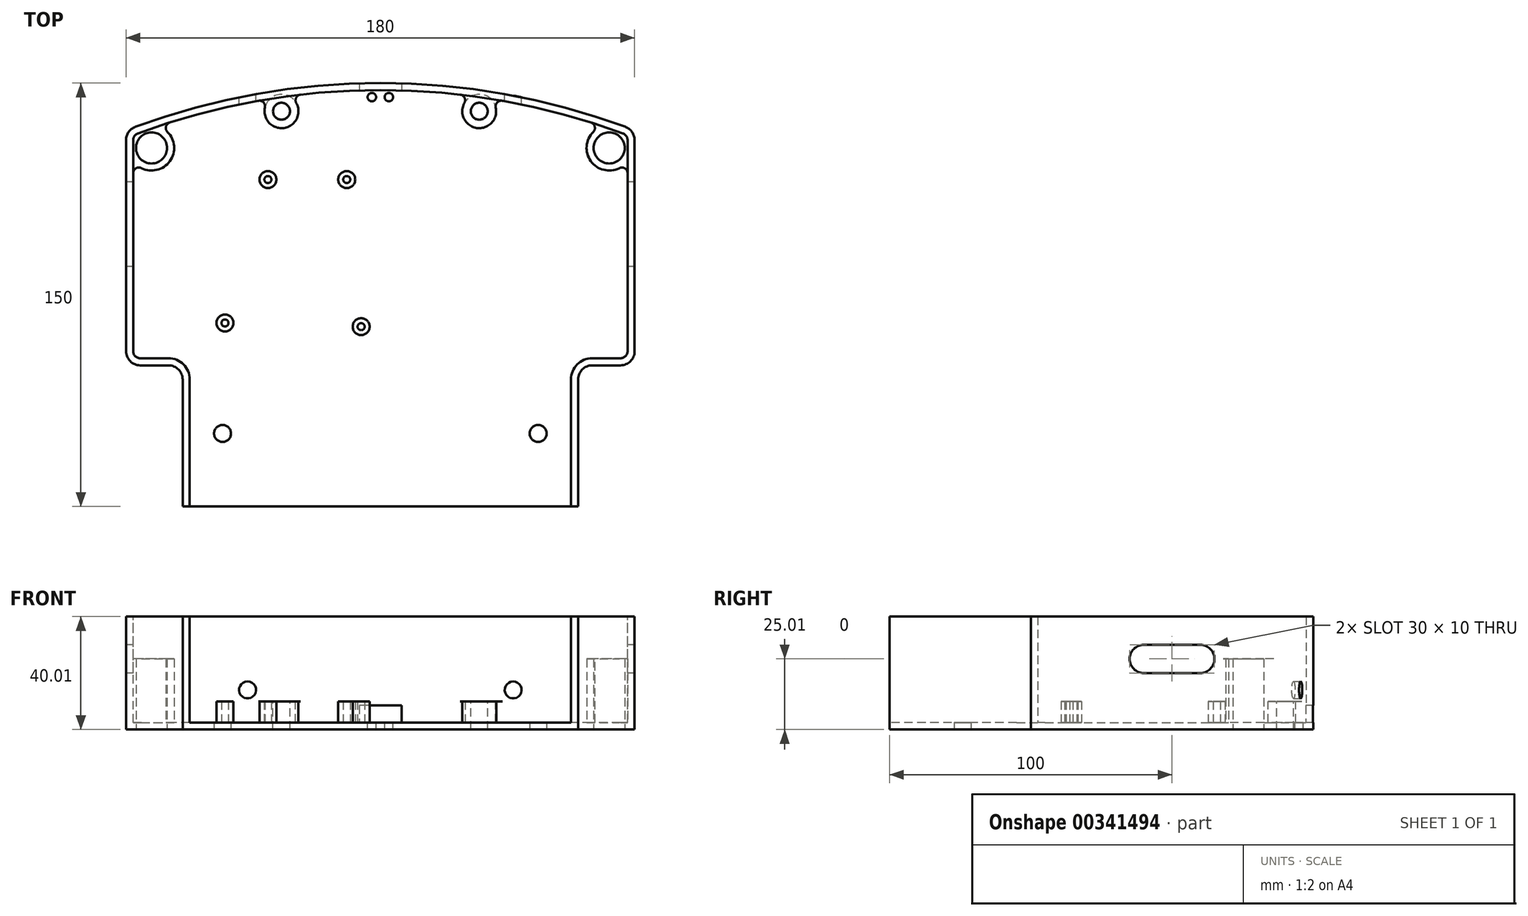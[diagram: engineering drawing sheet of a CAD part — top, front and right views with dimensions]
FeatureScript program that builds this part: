
annotation { "Feature Type Name" : "Feature", "Feature Type Description" : "" }
export const myFeature = defineFeature(function(context is Context, id is Id, definition is map)
    precondition{}
    {
        {
            var Q0;
            Q0=qCreatedBy(makeId("Top.planeOp"),FACE);
            var sketch = newSketch(context, id + "F0", { "sketchPlane" : qUnion([Q0])});
            skLineSegment(sketch, "E0.bottom", {"start": v(-90, -50) * mm, "end": v(90, -50) * mm});
            skLineSegment(sketch, "E0.top", {"start": v(-90, 100) * mm, "end": v(90, 100) * mm});
            skLineSegment(sketch, "E0.left", {"start": v(-90, -50) * mm, "end": v(-90, 100) * mm});
            skLineSegment(sketch, "E0.right", {"start": v(90, -50) * mm, "end": v(90, 100) * mm});
            skCircle(sketch, "E1", {"center": v(0, -150) * mm, "radius": 250 * mm});
            skSolve(sketch);
        }
        {
            var Q0;
            {var subQ4=sQuery(id+"F0.wireOp",EDGE,"E0.bottom");Q0=makeQuery(id+"F0.imprint","IMPRINT",FACE,{"disambiguationData":[TD([[makeQuery(id+"F0.imprint","IMPRINT",EDGE,{"derivedFrom":subQ4}),1.0]])]});}
            extrude(context, id + "F1", {"entities" : qUnion([Q0]), "depth" : 40 * mm});
        }
        {
            var Q0;
            Q0=qCreatedBy(makeId("Top.planeOp"),FACE);
            var sketch = newSketch(context, id + "F2", { "sketchPlane" : qUnion([Q0])});
            skLineSegment(sketch, "E2.bottom", {"start": v(-170, 0) * mm, "end": v(-70, 0) * mm});
            skLineSegment(sketch, "E2.top", {"start": v(-170, -200) * mm, "end": v(-70, -200) * mm});
            skLineSegment(sketch, "E2.left", {"start": v(-170, 0) * mm, "end": v(-170, -200) * mm});
            skLineSegment(sketch, "E2.right", {"start": v(-70, 0) * mm, "end": v(-70, -200) * mm});
            skLineSegment(sketch, "E3.bottom", {"start": v(170, 0) * mm, "end": v(70, 0) * mm});
            skLineSegment(sketch, "E3.top", {"start": v(170, -200) * mm, "end": v(70, -200) * mm});
            skLineSegment(sketch, "E3.left", {"start": v(170, 0) * mm, "end": v(170, -200) * mm});
            skLineSegment(sketch, "E3.right", {"start": v(70, 0) * mm, "end": v(70, -200) * mm});
            skSolve(sketch);
        }
        {
            var Q0;
            Q0=makeQuery(id+"F2.imprint","IMPRINT",FACE,{"disambiguationData":[TD([[makeQuery(id+"F2.imprint","IMPRINT",EDGE,{"derivedFrom":sQuery(id+"F2.wireOp",EDGE,"E2.bottom")}),-1.0]])]});
            var Q1;
            Q1=makeQuery(id+"F2.imprint","IMPRINT",FACE,{"disambiguationData":[TD([[makeQuery(id+"F2.imprint","IMPRINT",EDGE,{"derivedFrom":sQuery(id+"F2.wireOp",EDGE,"E3.bottom")}),1.0]])]});
            extrude(context, id + "F3", {"entities" : qUnion([Q0, Q1]), "operationType" : NewBodyOperationType.REMOVE, "depth" : 100 * mm});
        }
        {
            var Q0;
            Q0=makeQuery(id+"F1.opExtrude","SWEPT_EDGE",EDGE,{"disambiguationData":[OSD([sQuery(id+"F0.wireOp",EDGE,"E0.left"),sQuery(id+"F0.wireOp",EDGE,"E1")])]});
            var Q1;
            Q1=makeQuery(id+"F1.opExtrude","SWEPT_EDGE",EDGE,{"disambiguationData":[OSD([sQuery(id+"F0.wireOp",EDGE,"E0.right"),sQuery(id+"F0.wireOp",EDGE,"E1")])]});
            var Q2;
            Q2=makeQuery(id+"F3.boolean.opBoolean","INTERSECT",EDGE,{"derivedFrom":[makeQuery(id+"F1.opExtrude","SWEPT_FACE",FACE,{"disambiguationData":[OSD([sQuery(id+"F0.wireOp",EDGE,"E0.right")])]}),makeQuery(id+"F3.opExtrude","SWEPT_FACE",FACE,{"disambiguationData":[OSD([sQuery(id+"F2.wireOp",EDGE,"E3.bottom")])]})]});
            var Q3;
            Q3=makeQuery(id+"F3.boolean.opBoolean","COPY",EDGE,{"derivedFrom":makeQuery(id+"F3.opExtrude","SWEPT_EDGE",EDGE,{"disambiguationData":[OSD([sQuery(id+"F2.wireOp",EDGE,"E3.bottom"),sQuery(id+"F2.wireOp",EDGE,"E3.right")])]})});
            var Q4;
            Q4=makeQuery(id+"F3.boolean.opBoolean","INTERSECT",EDGE,{"derivedFrom":[makeQuery(id+"F1.opExtrude","SWEPT_FACE",FACE,{"disambiguationData":[OSD([sQuery(id+"F0.wireOp",EDGE,"E0.left")])]}),makeQuery(id+"F3.opExtrude","SWEPT_FACE",FACE,{"disambiguationData":[OSD([sQuery(id+"F2.wireOp",EDGE,"E2.bottom")])]})]});
            var Q5;
            Q5=makeQuery(id+"F3.boolean.opBoolean","COPY",EDGE,{"derivedFrom":makeQuery(id+"F3.opExtrude","SWEPT_EDGE",EDGE,{"disambiguationData":[OSD([sQuery(id+"F2.wireOp",EDGE,"E2.bottom"),sQuery(id+"F2.wireOp",EDGE,"E2.right")])]})});
            fillet(context, id + "F4", {"entities" : qUnion([Q0, Q1, Q2, Q3, Q4, Q5]), "radius" : 5 * mm, "tangentPropagation" : true, "allowEdgeOverflow" : false});
        }
        {
            var Q0;
            Q0=makeQuery(id+"F1.opExtrude","CAP_FACE",FACE,{"disambiguationData":[OSD([sQuery(id+"F0.wireOp",EDGE,"E0.bottom"),sQuery(id+"F0.wireOp",EDGE,"E0.left"),sQuery(id+"F0.wireOp",EDGE,"E0.right"),sQuery(id+"F0.wireOp",EDGE,"E1")])],"isStart":false});
            var Q1;
            Q1=makeQuery(id+"F1.opExtrude","SWEPT_FACE",FACE,{"disambiguationData":[OSD([sQuery(id+"F0.wireOp",EDGE,"E0.bottom")])]});
            shell(context, id + "F5", {"entities" : qUnion([Q0, Q1]), "thickness" : 2.5 * mm});
        }
        {
            var Q0;
            Q0=qCreatedBy(makeId("Top.planeOp"),FACE);
            var sketch = newSketch(context, id + "F6", { "sketchPlane" : qUnion([Q0])});
            skCircle(sketch, "E4", {"center": v(-55.86, -24.14) * mm, "radius": 3 * mm});
            skCircle(sketch, "E5", {"center": v(55.86, -24.14) * mm, "radius": 3 * mm});
            skLineSegment(sketch, "E6", {"start": v(0, -80) * mm, "end": v(-55.86, -24.14) * mm, "construction": true});
            skLineSegment(sketch, "E7", {"start": v(0, -80) * mm, "end": v(55.86, -24.14) * mm, "construction": true});
            skSolve(sketch);
        }
        {
            var Q0;
            Q0=qSketchRegion(id+"F6",true);
            extrude(context, id + "F7", {"entities" : qUnion([Q0]), "operationType" : NewBodyOperationType.REMOVE, "depth" : 25 * mm});
        }
        {
            var Q0;
            Q0=qCreatedBy(makeId("Top.planeOp"),FACE);
            var sketch = newSketch(context, id + "F8", { "sketchPlane" : qUnion([Q0])});
            skCircle(sketch, "E8", {"center": v(-81, 77) * mm, "radius": 8 * mm});
            skCircle(sketch, "E9", {"center": v(81, 77) * mm, "radius": 8 * mm});
            skSolve(sketch);
        }
        {
            var Q0;
            Q0=qSketchRegion(id+"F8",true);
            extrude(context, id + "F9", {"entities" : qUnion([Q0]), "operationType" : NewBodyOperationType.ADD, "depth" : 25 * mm});
        }
        {
            var Q0;
            Q0=qCreatedBy(makeId("Top.planeOp"),FACE);
            var sketch = newSketch(context, id + "F10", { "sketchPlane" : qUnion([Q0])});
            skCircle(sketch, "E10", {"center": v(-81, 77) * mm, "radius": 5.5 * mm});
            skCircle(sketch, "E11", {"center": v(81, 77) * mm, "radius": 5.5 * mm});
            skSolve(sketch);
        }
        {
            var Q0;
            Q0=qSketchRegion(id+"F10",true);
            extrude(context, id + "F11", {"entities" : qUnion([Q0]), "operationType" : NewBodyOperationType.REMOVE, "depth" : 25 * mm});
        }
        {
            var Q0;
            Q0=qCreatedBy(makeId("Top.planeOp"),FACE);
            var sketch = newSketch(context, id + "F12", { "sketchPlane" : qUnion([Q0])});
            skCircle(sketch, "E12", {"center": v(-55, 15) * mm, "radius": 3 * mm});
            skCircle(sketch, "E13", {"center": v(-55, 15) * mm, "radius": 1.25 * mm});
            skCircle(sketch, "E14", {"center": v(-39.8, 65.8) * mm, "radius": 1.25 * mm});
            skCircle(sketch, "E15", {"center": v(-39.8, 65.8) * mm, "radius": 3 * mm});
            skCircle(sketch, "E16", {"center": v(-11.9, 65.8) * mm, "radius": 1.25 * mm});
            skCircle(sketch, "E17", {"center": v(-11.9, 65.8) * mm, "radius": 3 * mm});
            skCircle(sketch, "E18", {"center": v(-6.8, 13.7) * mm, "radius": 1.25 * mm});
            skCircle(sketch, "E19", {"center": v(-6.8, 13.7) * mm, "radius": 3 * mm});
            skSolve(sketch);
        }
        {
            var Q0;
            Q0=qSketchRegion(id+"F12",true);
            extrude(context, id + "F13", {"entities" : qUnion([Q0]), "operationType" : NewBodyOperationType.ADD, "depth" : 10 * mm});
        }
        {
            var Q0;
            Q0=qCreatedBy(makeId("Front.planeOp"),FACE);
            var sketch = newSketch(context, id + "F14", { "sketchPlane" : qUnion([Q0])});
            skCircle(sketch, "E20", {"center": v(47, 14) * mm, "radius": 3 * mm});
            skCircle(sketch, "E21", {"center": v(-47, 14) * mm, "radius": 3 * mm});
            skSolve(sketch);
        }
        {
            var Q0;
            Q0=qSketchRegion(id+"F14",true);
            extrude(context, id + "F15", {"entities" : qUnion([Q0]), "operationType" : NewBodyOperationType.REMOVE, "endBound" : BoundingType.SYMMETRIC, "depth" : 300 * mm});
        }
        {
            var Q0;
            Q0=qCreatedBy(makeId("Front.planeOp"),FACE);
            var sketch = newSketch(context, id + "F16", { "sketchPlane" : qUnion([Q0])});
            skLineSegment(sketch, "E22.bottom", {"start": v(7.5, 8.5) * mm, "end": v(-7.5, 8.5) * mm});
            skLineSegment(sketch, "E22.top", {"start": v(7.5, 2.5) * mm, "end": v(-7.5, 2.5) * mm});
            skLineSegment(sketch, "E22.left", {"start": v(7.5, 8.5) * mm, "end": v(7.5, 2.5) * mm});
            skLineSegment(sketch, "E22.right", {"start": v(-7.5, 8.5) * mm, "end": v(-7.5, 2.5) * mm});
            skSolve(sketch);
        }
        {
            var Q0;
            Q0=makeQuery(id+"F16.imprint","IMPRINT",FACE,{"disambiguationData":[TD([[makeQuery(id+"F16.imprint","IMPRINT",EDGE,{"derivedFrom":sQuery(id+"F16.wireOp",EDGE,"E22.bottom")}),1.0]])]});
            extrude(context, id + "F17", {"entities" : qUnion([Q0]), "operationType" : NewBodyOperationType.REMOVE, "oppositeDirection" : true, "depth" : 250 * mm, "hasSecondDirection" : true, "secondDirectionOppositeDirection" : true, "secondDirectionDepth" : 41.95 * mm});
        }
        {
            var Q0;
            Q0=qCreatedBy(makeId("Top.planeOp"),FACE);
            var sketch = newSketch(context, id + "F18", { "sketchPlane" : qUnion([Q0])});
            skCircle(sketch, "E23", {"center": v(3, 95) * mm, "radius": 1.5 * mm});
            skCircle(sketch, "E24", {"center": v(-3, 95) * mm, "radius": 1.5 * mm});
            skSolve(sketch);
        }
        {
            var Q0;
            Q0=makeQuery(id+"F18.imprint","IMPRINT",FACE,{"disambiguationData":[TD([[makeQuery(id+"F18.imprint","IMPRINT",EDGE,{"derivedFrom":sQuery(id+"F18.wireOp",EDGE,"E24")}),1.0]])]});
            var Q1;
            Q1=makeQuery(id+"F18.imprint","IMPRINT",FACE,{"disambiguationData":[TD([[makeQuery(id+"F18.imprint","IMPRINT",EDGE,{"derivedFrom":sQuery(id+"F18.wireOp",EDGE,"E23")}),1.0]])]});
            extrude(context, id + "F19", {"entities" : qUnion([Q0, Q1]), "operationType" : NewBodyOperationType.REMOVE, "endBound" : BoundingType.SYMMETRIC, "oppositeDirection" : true, "depth" : 25 * mm});
        }
        {
            var Q0;
            Q0=qCreatedBy(makeId("Top.planeOp"),FACE);
            var sketch = newSketch(context, id + "F20", { "sketchPlane" : qUnion([Q0])});
            skCircle(sketch, "E25", {"center": v(-35, 90) * mm, "radius": 6 * mm});
            skCircle(sketch, "E26", {"center": v(35, 90) * mm, "radius": 6 * mm});
            skSolve(sketch);
        }
        {
            var Q0;
            Q0=qSketchRegion(id+"F20",true);
            extrude(context, id + "F21", {"entities" : qUnion([Q0]), "operationType" : NewBodyOperationType.ADD, "oppositeDirection" : true, "depth" : 0.01 * mm, "hasSecondDirection" : true, "secondDirectionOppositeDirection" : false, "secondDirectionDepth" : 10 * mm});
        }
        {
            var Q0;
            Q0=makeQuery(id+"F1.opExtrude","CAP_FACE",FACE,{"disambiguationData":[OSD([sQuery(id+"F0.wireOp",EDGE,"E0.bottom"),sQuery(id+"F0.wireOp",EDGE,"E0.left"),sQuery(id+"F0.wireOp",EDGE,"E0.right"),sQuery(id+"F0.wireOp",EDGE,"E1")])],"isStart":true});
            var sketch = newSketch(context, id + "F22", { "sketchPlane" : qUnion([Q0])});
            skCircle(sketch, "E27", {"center": v(-35, -90) * mm, "radius": 3 * mm});
            skCircle(sketch, "E28", {"center": v(35, -90) * mm, "radius": 3 * mm});
            skSolve(sketch);
        }
        {
            var Q0;
            Q0=qSketchRegion(id+"F22",true);
            extrude(context, id + "F23", {"entities" : qUnion([Q0]), "operationType" : NewBodyOperationType.REMOVE, "endBound" : BoundingType.SYMMETRIC, "depth" : 25 * mm});
        }
        {
            var Q0;
            Q0=makeQuery(id+"F9.boolean.opBoolean","INTERSECT",EDGE,{"derivedFrom":[makeQuery(id+"F5.opShell","OFFSET_FACE",FACE,{"disambiguationData":[OSD([sQuery(id+"F0.wireOp",EDGE,"E0.left")])]}),makeQuery(id+"F9.opExtrude","SWEPT_FACE",FACE,{"disambiguationData":[OSD([sQuery(id+"F8.wireOp",EDGE,"E8")])]})]});
            var Q1;
            Q1=makeQuery(id+"F9.boolean.opBoolean","INTERSECT",EDGE,{"derivedFrom":[makeQuery(id+"F5.opShell","OFFSET_FACE",FACE,{"disambiguationData":[OSD([sQuery(id+"F0.wireOp",EDGE,"E1")])]}),makeQuery(id+"F9.opExtrude","SWEPT_FACE",FACE,{"disambiguationData":[OSD([sQuery(id+"F8.wireOp",EDGE,"E8")])]})]});
            var Q2;
            Q2=makeQuery(id+"F21.boolean.opBoolean","INTERSECT",EDGE,{"disambiguationData":[OD(0.0)],"derivedFrom":[makeQuery(id+"F5.opShell","OFFSET_FACE",FACE,{"disambiguationData":[OSD([sQuery(id+"F0.wireOp",EDGE,"E1")])]}),makeQuery(id+"F21.opExtrude","SWEPT_FACE",FACE,{"disambiguationData":[OSD([sQuery(id+"F20.wireOp",EDGE,"E25")])]})]});
            var Q3;
            Q3=makeQuery(id+"F21.boolean.opBoolean","INTERSECT",EDGE,{"disambiguationData":[OD(1.0)],"derivedFrom":[makeQuery(id+"F5.opShell","OFFSET_FACE",FACE,{"disambiguationData":[OSD([sQuery(id+"F0.wireOp",EDGE,"E1")])]}),makeQuery(id+"F21.opExtrude","SWEPT_FACE",FACE,{"disambiguationData":[OSD([sQuery(id+"F20.wireOp",EDGE,"E25")])]})]});
            var Q4;
            Q4=makeQuery(id+"F21.boolean.opBoolean","INTERSECT",EDGE,{"disambiguationData":[OD(1.0)],"derivedFrom":[makeQuery(id+"F5.opShell","OFFSET_FACE",FACE,{"disambiguationData":[OSD([sQuery(id+"F0.wireOp",EDGE,"E1")])]}),makeQuery(id+"F21.opExtrude","SWEPT_FACE",FACE,{"disambiguationData":[OSD([sQuery(id+"F20.wireOp",EDGE,"E26")])]})]});
            var Q5;
            Q5=makeQuery(id+"F21.boolean.opBoolean","INTERSECT",EDGE,{"disambiguationData":[OD(0.0)],"derivedFrom":[makeQuery(id+"F5.opShell","OFFSET_FACE",FACE,{"disambiguationData":[OSD([sQuery(id+"F0.wireOp",EDGE,"E1")])]}),makeQuery(id+"F21.opExtrude","SWEPT_FACE",FACE,{"disambiguationData":[OSD([sQuery(id+"F20.wireOp",EDGE,"E26")])]})]});
            var Q6;
            Q6=makeQuery(id+"F9.boolean.opBoolean","INTERSECT",EDGE,{"derivedFrom":[makeQuery(id+"F5.opShell","OFFSET_FACE",FACE,{"disambiguationData":[OSD([sQuery(id+"F0.wireOp",EDGE,"E1")])]}),makeQuery(id+"F9.opExtrude","SWEPT_FACE",FACE,{"disambiguationData":[OSD([sQuery(id+"F8.wireOp",EDGE,"E9")])]})]});
            var Q7;
            Q7=makeQuery(id+"F9.boolean.opBoolean","INTERSECT",EDGE,{"derivedFrom":[makeQuery(id+"F5.opShell","OFFSET_FACE",FACE,{"disambiguationData":[OSD([sQuery(id+"F0.wireOp",EDGE,"E0.right")])]}),makeQuery(id+"F9.opExtrude","SWEPT_FACE",FACE,{"disambiguationData":[OSD([sQuery(id+"F8.wireOp",EDGE,"E9")])]})]});
            fillet(context, id + "F24", {"entities" : qUnion([Q0, Q1, Q2, Q3, Q4, Q5, Q6, Q7]), "radius" : 2 * mm, "tangentPropagation" : true, "allowEdgeOverflow" : false});
        }
        {
            var Q0;
            Q0=qCreatedBy(makeId("Right.planeOp"),FACE);
            var sketch = newSketch(context, id + "F25", { "sketchPlane" : qUnion([Q0])});
            skLineSegment(sketch, "E29.bottom", {"start": v(40, 30) * mm, "end": v(60, 30) * mm});
            skLineSegment(sketch, "E29.top", {"start": v(40, 20) * mm, "end": v(60, 20) * mm});
            skLineSegment(sketch, "E29.left", {"start": v(40, 30) * mm, "end": v(40, 20) * mm});
            skLineSegment(sketch, "E29.right", {"start": v(60, 30) * mm, "end": v(60, 20) * mm});
            skCircle(sketch, "E30", {"center": v(40, 25) * mm, "radius": 5 * mm});
            skCircle(sketch, "E31", {"center": v(60, 25) * mm, "radius": 5 * mm});
            skSolve(sketch);
        }
        {
            var Q0;
            {var subQ0=sQuery(id+"F25.wireOp",EDGE,"E29.left");Q0=makeQuery(id+"F25.imprint","IMPRINT",FACE,{"disambiguationData":[TD([[makeQuery(id+"F25.imprint","IMPRINT",EDGE,{"derivedFrom":subQ0}),-1.0]])]});}
            var Q1;
            {var subQ0=sQuery(id+"F25.wireOp",EDGE,"E29.right");Q1=makeQuery(id+"F25.imprint","IMPRINT",FACE,{"disambiguationData":[TD([[makeQuery(id+"F25.imprint","IMPRINT",EDGE,{"derivedFrom":subQ0}),1.0]])]});}
            var Q2;
            {var subQ0=sQuery(id+"F25.wireOp",EDGE,"E29.bottom");Q2=makeQuery(id+"F25.imprint","IMPRINT",FACE,{"disambiguationData":[TD([[makeQuery(id+"F25.imprint","IMPRINT",EDGE,{"derivedFrom":subQ0}),-1.0]])]});}
            var Q3;
            {var subQ0=sQuery(id+"F25.wireOp",EDGE,"E29.left");Q3=makeQuery(id+"F25.imprint","IMPRINT",FACE,{"disambiguationData":[TD([[makeQuery(id+"F25.imprint","IMPRINT",EDGE,{"derivedFrom":subQ0}),1.0]])]});}
            var Q4;
            {var subQ0=sQuery(id+"F25.wireOp",EDGE,"E29.right");Q4=makeQuery(id+"F25.imprint","IMPRINT",FACE,{"disambiguationData":[TD([[makeQuery(id+"F25.imprint","IMPRINT",EDGE,{"derivedFrom":subQ0}),-1.0]])]});}
            extrude(context, id + "F26", {"entities" : qUnion([Q0, Q1, Q2, Q3, Q4]), "operationType" : NewBodyOperationType.REMOVE, "endBound" : BoundingType.SYMMETRIC, "depth" : 300 * mm});
        }
    });
